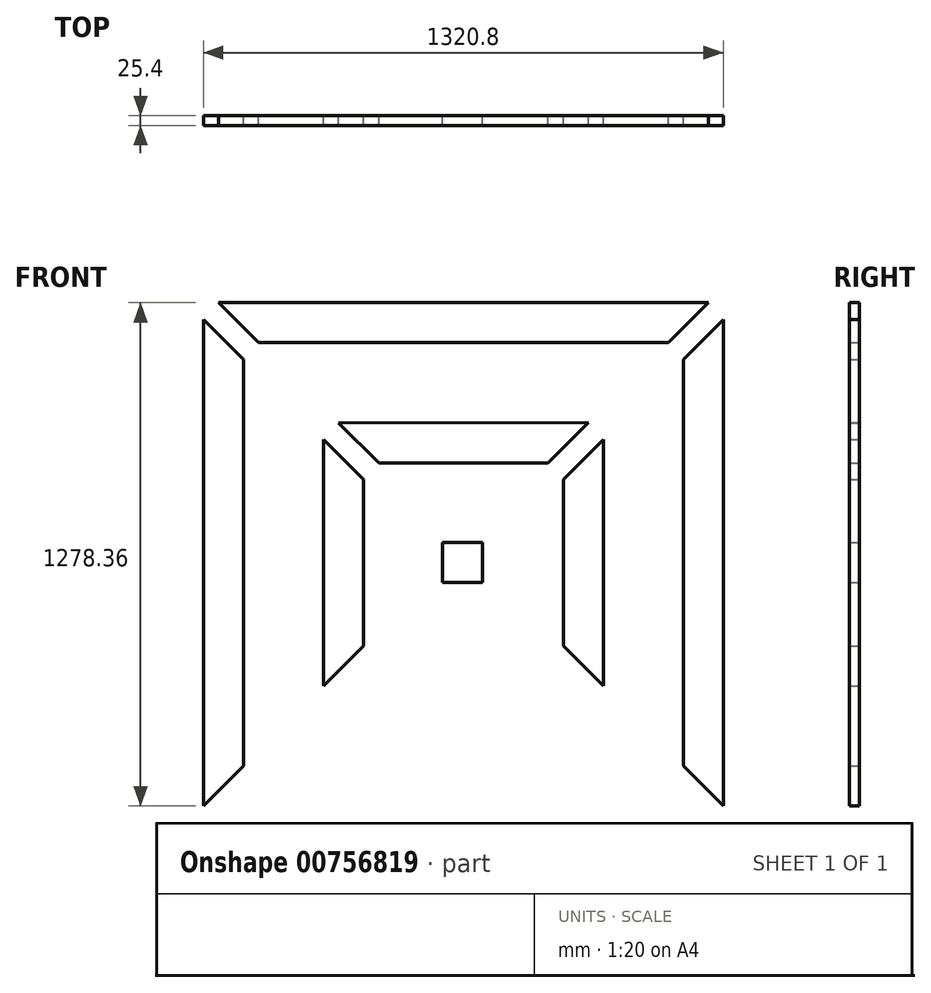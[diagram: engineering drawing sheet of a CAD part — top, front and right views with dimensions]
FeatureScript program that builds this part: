
annotation { "Feature Type Name" : "Feature", "Feature Type Description" : "" }
export const myFeature = defineFeature(function(context is Context, id is Id, definition is map)
    precondition{}
    {
        {
            var Q0;
            Q0=qCreatedBy(makeId("Front.planeOp"),FACE);
            var sketch = newSketch(context, id + "F0", { "sketchPlane" : qUnion([Q0])});
            skLineSegment(sketch, "E0.bottom", {"start": v(1332.07, -71.9) * mm, "end": v(1205.07, -71.9) * mm});
            skLineSegment(sketch, "E0.top", {"start": v(1332.07, -198.9) * mm, "end": v(1205.07, -198.9) * mm});
            skLineSegment(sketch, "E0.left", {"start": v(1332.07, -71.9) * mm, "end": v(1332.07, -198.9) * mm});
            skLineSegment(sketch, "E0.right", {"start": v(1205.07, -71.9) * mm, "end": v(1205.07, -198.9) * mm});
            skPoint(sketch, "E0.middle", {"position": v(1268.57, -135.4) * mm});
            skLineSegment(sketch, "E1", {"start": v(1268.57, -71.9) * mm, "end": v(1268.57, -46.5) * mm});
            skLineSegment(sketch, "E2", {"start": v(1268.57, -46.5) * mm, "end": v(1268.57, 80.5) * mm});
            skLineSegment(sketch, "E3", {"start": v(1268.57, 80.5) * mm, "end": v(1268.57, 105.9) * mm});
            skLineSegment(sketch, "E4", {"start": v(1205.07, -135.4) * mm, "end": v(1179.67, -135.4) * mm});
            skLineSegment(sketch, "E5", {"start": v(1179.67, -135.4) * mm, "end": v(1054.23, -135.4) * mm});
            skLineSegment(sketch, "E6", {"start": v(901.83, -135.4) * mm, "end": v(876.43, -135.4) * mm});
            skLineSegment(sketch, "E7", {"start": v(571.63, -135.4) * mm, "end": v(571.63, 563.1) * mm});
            skLineSegment(sketch, "E8", {"start": v(571.63, 563.1) * mm, "end": v(1268.57, 563.1) * mm});
            skLineSegment(sketch, "E9", {"start": v(1268.57, 537.7) * mm, "end": v(597.03, 537.7) * mm});
            skLineSegment(sketch, "E10", {"start": v(597.03, 537.7) * mm, "end": v(597.03, -135.4) * mm});
            skLineSegment(sketch, "E11", {"start": v(724.03, -135.4) * mm, "end": v(724.03, 410.7) * mm});
            skLineSegment(sketch, "E12", {"start": v(724.03, 410.7) * mm, "end": v(1268.57, 410.7) * mm});
            skLineSegment(sketch, "E13", {"start": v(1268.57, 385.3) * mm, "end": v(749.43, 385.3) * mm});
            skLineSegment(sketch, "E14", {"start": v(749.43, 385.3) * mm, "end": v(749.43, -135.4) * mm});
            skLineSegment(sketch, "E15", {"start": v(876.43, -135.4) * mm, "end": v(876.43, 258.3) * mm});
            skLineSegment(sketch, "E16", {"start": v(876.43, 258.3) * mm, "end": v(1268.57, 258.3) * mm});
            skLineSegment(sketch, "E17", {"start": v(1268.57, 232.9) * mm, "end": v(901.83, 232.9) * mm});
            skLineSegment(sketch, "E18", {"start": v(901.83, 232.9) * mm, "end": v(901.83, -135.4) * mm});
            skLineSegment(sketch, "E19", {"start": v(1028.83, -135.4) * mm, "end": v(1028.83, 105.9) * mm});
            skLineSegment(sketch, "E20", {"start": v(1028.83, 105.9) * mm, "end": v(1268.57, 105.9) * mm});
            skLineSegment(sketch, "E21", {"start": v(1268.57, 80.5) * mm, "end": v(1054.23, 80.5) * mm});
            skLineSegment(sketch, "E22", {"start": v(1054.23, 80.5) * mm, "end": v(1054.23, -135.4) * mm});
            skLineSegment(sketch, "E23", {"start": v(1179.67, -135.4) * mm, "end": v(1179.67, -46.5) * mm});
            skLineSegment(sketch, "E24", {"start": v(1179.67, -46.5) * mm, "end": v(1268.57, -46.5) * mm});
            skLineSegment(sketch, "E25", {"start": v(578.07, 533.09) * mm, "end": v(1181.32, -70.16) * mm});
            skLineSegment(sketch, "E26", {"start": v(1200.28, -46.5) * mm, "end": v(597.03, 556.74) * mm});
            skLineSegment(sketch, "E27.MirrorCS", {"start": v(1359.03, -46.5) * mm, "end": v(1270.13, -46.5) * mm});
            skLineSegment(sketch, "E28.MirrorCS", {"start": v(1339.98, -46.5) * mm, "end": v(1943.23, 556.74) * mm});
            skLineSegment(sketch, "E29.MirrorCS", {"start": v(1962.2, 533.09) * mm, "end": v(1358.94, -70.16) * mm});
            skLineSegment(sketch, "E30.MirrorCS", {"start": v(1270.13, 80.5) * mm, "end": v(1486.03, 80.5) * mm});
            skLineSegment(sketch, "E31.MirrorCS", {"start": v(1511.43, 105.9) * mm, "end": v(1270.13, 105.9) * mm});
            skLineSegment(sketch, "E32.MirrorCS", {"start": v(1270.13, 232.9) * mm, "end": v(1638.43, 232.9) * mm});
            skLineSegment(sketch, "E33.MirrorCS", {"start": v(1663.84, 258.3) * mm, "end": v(1270.14, 258.3) * mm});
            skLineSegment(sketch, "E34.MirrorCS", {"start": v(1270.14, 385.3) * mm, "end": v(1790.84, 385.3) * mm});
            skLineSegment(sketch, "E35.MirrorCS", {"start": v(1816.24, 410.7) * mm, "end": v(1270.14, 410.7) * mm});
            skLineSegment(sketch, "E36.MirrorCS", {"start": v(1270.13, 537.7) * mm, "end": v(1943.23, 537.7) * mm});
            skLineSegment(sketch, "E37.MirrorCS", {"start": v(1968.63, 563.1) * mm, "end": v(1270.13, 563.1) * mm});
            skLineSegment(sketch, "E38.MirrorCS", {"start": v(1968.63, -135.4) * mm, "end": v(1968.63, 563.1) * mm});
            skLineSegment(sketch, "E39.MirrorCS", {"start": v(1943.23, 537.7) * mm, "end": v(1943.23, -135.4) * mm});
            skLineSegment(sketch, "E40.MirrorCS", {"start": v(1663.83, -135.4) * mm, "end": v(1663.83, 258.3) * mm});
            skLineSegment(sketch, "E41.MirrorCS", {"start": v(1638.43, 232.9) * mm, "end": v(1638.43, -135.4) * mm});
            skLineSegment(sketch, "E42.MirrorCS", {"start": v(1511.43, -135.4) * mm, "end": v(1511.43, 105.9) * mm});
            skLineSegment(sketch, "E43.MirrorCS", {"start": v(1486.03, 80.5) * mm, "end": v(1486.03, -135.4) * mm});
            skLineSegment(sketch, "E44.MirrorCS", {"start": v(1359.03, -135.4) * mm, "end": v(1359.03, -46.5) * mm});
            skLineSegment(sketch, "E45.MirrorCS", {"start": v(1333.63, -71.9) * mm, "end": v(1333.63, -198.9) * mm});
            skLineSegment(sketch, "E46.MirrorCS", {"start": v(1790.83, 385.3) * mm, "end": v(1790.83, -135.4) * mm});
            skLineSegment(sketch, "E47.MirrorCS", {"start": v(1816.23, -135.4) * mm, "end": v(1816.23, 410.7) * mm});
            skLineSegment(sketch, "E48.MirrorCS", {"start": v(597.03, -808.5) * mm, "end": v(597.03, -135.4) * mm});
            skLineSegment(sketch, "E49.MirrorCS", {"start": v(724.03, -135.4) * mm, "end": v(724.03, -681.5) * mm});
            skLineSegment(sketch, "E50.MirrorCS", {"start": v(749.43, -656.1) * mm, "end": v(749.43, -135.4) * mm});
            skLineSegment(sketch, "E51.MirrorCS", {"start": v(876.43, -135.4) * mm, "end": v(876.43, -529.1) * mm});
            skLineSegment(sketch, "E52.MirrorCS", {"start": v(901.83, -503.7) * mm, "end": v(901.83, -135.4) * mm});
            skLineSegment(sketch, "E53.MirrorCS", {"start": v(1028.83, -135.4) * mm, "end": v(1028.83, -376.7) * mm});
            skLineSegment(sketch, "E54.MirrorCS", {"start": v(1054.23, -351.3) * mm, "end": v(1054.23, -135.4) * mm});
            skLineSegment(sketch, "E55.MirrorCS", {"start": v(1181.23, -135.4) * mm, "end": v(1181.23, -224.3) * mm});
            skLineSegment(sketch, "E56.MirrorCS", {"start": v(1206.63, -198.9) * mm, "end": v(1206.63, -71.9) * mm});
            skLineSegment(sketch, "E57.MirrorCS", {"start": v(1333.63, -198.9) * mm, "end": v(1333.63, -71.9) * mm});
            skLineSegment(sketch, "E58.MirrorCS", {"start": v(1359.03, -135.4) * mm, "end": v(1359.03, -224.3) * mm});
            skLineSegment(sketch, "E59.MirrorCS", {"start": v(1486.03, -351.3) * mm, "end": v(1486.03, -135.4) * mm});
            skLineSegment(sketch, "E60.MirrorCS", {"start": v(1511.43, -135.4) * mm, "end": v(1511.43, -376.7) * mm});
            skLineSegment(sketch, "E61.MirrorCS", {"start": v(1638.43, -503.7) * mm, "end": v(1638.43, -135.4) * mm});
            skLineSegment(sketch, "E62.MirrorCS", {"start": v(1663.83, -135.4) * mm, "end": v(1663.83, -529.1) * mm});
            skLineSegment(sketch, "E63.MirrorCS", {"start": v(1790.83, -656.1) * mm, "end": v(1790.83, -135.4) * mm});
            skLineSegment(sketch, "E64.MirrorCS", {"start": v(1816.23, -135.4) * mm, "end": v(1816.23, -681.5) * mm});
            skLineSegment(sketch, "E65.MirrorCS", {"start": v(1943.23, -808.5) * mm, "end": v(1943.23, -135.4) * mm});
            skLineSegment(sketch, "E66.MirrorCS", {"start": v(1968.63, -135.4) * mm, "end": v(1968.63, -833.9) * mm});
            skLineSegment(sketch, "E67.MirrorCS", {"start": v(1962.2, -803.9) * mm, "end": v(1358.94, -200.65) * mm});
            skLineSegment(sketch, "E68.MirrorCS", {"start": v(1339.98, -224.3) * mm, "end": v(1943.23, -827.56) * mm});
            skLineSegment(sketch, "E69.MirrorCS", {"start": v(578.07, -803.9) * mm, "end": v(1181.32, -200.65) * mm});
            skLineSegment(sketch, "E70.MirrorCS", {"start": v(1270.13, -351.3) * mm, "end": v(1054.23, -351.3) * mm});
            skLineSegment(sketch, "E71.MirrorCS", {"start": v(1270.13, -351.3) * mm, "end": v(1486.03, -351.3) * mm});
            skLineSegment(sketch, "E72.MirrorCS", {"start": v(1663.83, -529.1) * mm, "end": v(1270.13, -529.1) * mm});
            skLineSegment(sketch, "E73.MirrorCS", {"start": v(876.43, -529.1) * mm, "end": v(1270.13, -529.1) * mm});
            skLineSegment(sketch, "E74.MirrorCS", {"start": v(1270.13, -503.7) * mm, "end": v(901.83, -503.7) * mm});
            skLineSegment(sketch, "E75.MirrorCS", {"start": v(1270.13, -503.7) * mm, "end": v(1638.43, -503.7) * mm});
            skLineSegment(sketch, "E76.MirrorCS", {"start": v(1270.13, -656.1) * mm, "end": v(1790.83, -656.1) * mm});
            skLineSegment(sketch, "E77.MirrorCS", {"start": v(1270.13, -656.1) * mm, "end": v(749.43, -656.1) * mm});
            skLineSegment(sketch, "E78.MirrorCS", {"start": v(724.03, -681.5) * mm, "end": v(1270.13, -681.5) * mm});
            skLineSegment(sketch, "E79.MirrorCS", {"start": v(1816.23, -681.5) * mm, "end": v(1270.13, -681.5) * mm});
            skLineSegment(sketch, "E80.MirrorCS", {"start": v(1270.13, -808.5) * mm, "end": v(1943.23, -808.5) * mm});
            skLineSegment(sketch, "E81.MirrorCS", {"start": v(1968.63, -833.9) * mm, "end": v(1270.13, -833.9) * mm});
            skLineSegment(sketch, "E82.MirrorCS", {"start": v(571.63, -833.9) * mm, "end": v(1270.13, -833.9) * mm});
            skLineSegment(sketch, "E83.MirrorCS", {"start": v(1270.13, -808.5) * mm, "end": v(597.03, -808.5) * mm});
            skLineSegment(sketch, "E84.MirrorCS", {"start": v(571.63, -135.4) * mm, "end": v(571.63, -833.9) * mm});
            skLineSegment(sketch, "E85.MirrorCS", {"start": v(1028.83, -376.7) * mm, "end": v(1270.13, -376.7) * mm});
            skLineSegment(sketch, "E86.MirrorCS", {"start": v(1511.43, -376.7) * mm, "end": v(1270.13, -376.7) * mm});
            skLineSegment(sketch, "E87.MirrorCS", {"start": v(1200.28, -224.3) * mm, "end": v(597.03, -827.56) * mm});
            skLineSegment(sketch, "E88.MirrorCS", {"start": v(1359.03, -224.3) * mm, "end": v(1270.13, -224.3) * mm});
            skLineSegment(sketch, "E89.MirrorCS", {"start": v(1181.23, -224.3) * mm, "end": v(1270.13, -224.3) * mm});
            skLineSegment(sketch, "E90", {"start": v(596.66, 514.5) * mm, "end": v(597.03, 495.46) * mm});
            skLineSegment(sketch, "E91", {"start": v(616.08, 537.7) * mm, "end": v(635.13, 537.48) * mm});
            skLineSegment(sketch, "E92", {"start": v(1047.88, 105.9) * mm, "end": v(1066.93, 105.9) * mm});
            skLineSegment(sketch, "E93", {"start": v(1028.83, 82.33) * mm, "end": v(1028.83, 63.28) * mm});
            skLineSegment(sketch, "E94", {"start": v(1028.83, 63.28) * mm, "end": v(597.03, 495.46) * mm});
            skLineSegment(sketch, "E95", {"start": v(635.13, 537.48) * mm, "end": v(1066.93, 105.9) * mm});
            skLineSegment(sketch, "E96", {"start": v(635.13, 537.48) * mm, "end": v(635.13, 518.64) * mm});
            skLineSegment(sketch, "E97", {"start": v(724.03, 368.34) * mm, "end": v(711.33, 368.34) * mm});
            skLineSegment(sketch, "E98", {"start": v(597.03, 495.46) * mm, "end": v(609.73, 495.46) * mm});
            skLineSegment(sketch, "E99", {"start": v(609.73, 495.46) * mm, "end": v(609.73, -135.4) * mm});
            skLineSegment(sketch, "E100", {"start": v(571.63, 563.1) * mm, "end": v(1205.07, -71.9) * mm});
            skLineSegment(sketch, "E101.bottom", {"start": v(1205.07, -71.9) * mm, "end": v(1217.77, -71.9) * mm});
            skLineSegment(sketch, "E101.top", {"start": v(1205.07, -84.6) * mm, "end": v(1217.77, -84.6) * mm});
            skLineSegment(sketch, "E101.left", {"start": v(1205.07, -71.9) * mm, "end": v(1205.07, -84.6) * mm});
            skLineSegment(sketch, "E101.right", {"start": v(1217.77, -71.9) * mm, "end": v(1217.77, -84.6) * mm});
            skLineSegment(sketch, "E102.bottom", {"start": v(1217.77, -84.6) * mm, "end": v(1268.57, -84.6) * mm});
            skLineSegment(sketch, "E102.top", {"start": v(1217.77, -135.4) * mm, "end": v(1268.57, -135.4) * mm});
            skLineSegment(sketch, "E102.left", {"start": v(1217.77, -84.6) * mm, "end": v(1217.77, -135.4) * mm});
            skLineSegment(sketch, "E102.right", {"start": v(1268.57, -84.6) * mm, "end": v(1268.57, -135.4) * mm});
            skLineSegment(sketch, "E103", {"start": v(1028.83, 63.28) * mm, "end": v(1016.13, 63.28) * mm});
            skLineSegment(sketch, "E104", {"start": v(1016.13, 63.28) * mm, "end": v(1016.13, 75.99) * mm});
            skLineSegment(sketch, "E105", {"start": v(1016.13, 75.99) * mm, "end": v(1016.13, -135.4) * mm});
            skLineSegment(sketch, "E106", {"start": v(901.83, 169.52) * mm, "end": v(914.53, 169.52) * mm});
            skLineSegment(sketch, "E107", {"start": v(914.53, 169.52) * mm, "end": v(914.53, 184.76) * mm});
            skLineSegment(sketch, "E108", {"start": v(914.53, 184.76) * mm, "end": v(914.53, -135.4) * mm});
            skLineSegment(sketch, "E109.MirrorCS", {"start": v(753.67, 423.4) * mm, "end": v(1270.13, 423.4) * mm});
            skLineSegment(sketch, "E110.MirrorCS", {"start": v(1217.73, -84.64) * mm, "end": v(1268.53, -84.76) * mm});
            skLineSegment(sketch, "E111.bottom", {"start": v(1332.07, -198.9) * mm, "end": v(1319.37, -198.9) * mm});
            skLineSegment(sketch, "E111.top", {"start": v(1332.07, -186.2) * mm, "end": v(1319.37, -186.2) * mm});
            skLineSegment(sketch, "E111.left", {"start": v(1332.07, -198.9) * mm, "end": v(1332.07, -186.2) * mm});
            skLineSegment(sketch, "E111.right", {"start": v(1319.37, -198.9) * mm, "end": v(1319.37, -186.2) * mm});
            skLineSegment(sketch, "E112.bottom", {"start": v(1217.77, -84.6) * mm, "end": v(1319.37, -84.6) * mm});
            skLineSegment(sketch, "E112.top", {"start": v(1217.77, -186.2) * mm, "end": v(1319.37, -186.2) * mm});
            skLineSegment(sketch, "E112.left", {"start": v(1217.77, -84.6) * mm, "end": v(1217.77, -186.2) * mm});
            skLineSegment(sketch, "E112.right", {"start": v(1319.37, -84.6) * mm, "end": v(1319.37, -186.2) * mm});
            skLineSegment(sketch, "E113.MirrorCS", {"start": v(1905.13, 537.48) * mm, "end": v(1473.33, 105.9) * mm});
            skLineSegment(sketch, "E114.MirrorCS", {"start": v(1786.6, 423.4) * mm, "end": v(1270.13, 423.4) * mm});
            skLineSegment(sketch, "E115.MirrorCS", {"start": v(1930.53, 495.46) * mm, "end": v(1930.53, -135.4) * mm});
            skLineSegment(sketch, "E116.MirrorCS", {"start": v(1828.93, 381.06) * mm, "end": v(1828.93, -135.4) * mm});
            skLineSegment(sketch, "E117.MirrorCS", {"start": v(1625.73, 184.76) * mm, "end": v(1625.73, -135.4) * mm});
            skLineSegment(sketch, "E118.MirrorCS", {"start": v(1524.13, 75.99) * mm, "end": v(1524.13, -135.4) * mm});
            skLineSegment(sketch, "E119.MirrorCS", {"start": v(1511.43, 63.28) * mm, "end": v(1943.23, 495.46) * mm});
            skLineSegment(sketch, "E120.MirrorCS", {"start": v(609.73, -766.27) * mm, "end": v(609.73, -135.4) * mm});
            skLineSegment(sketch, "E121.MirrorCS", {"start": v(711.33, -651.87) * mm, "end": v(711.33, -135.4) * mm});
            skLineSegment(sketch, "E122.MirrorCS", {"start": v(914.53, -455.58) * mm, "end": v(914.53, -135.4) * mm});
            skLineSegment(sketch, "E123.MirrorCS", {"start": v(1016.13, -346.8) * mm, "end": v(1016.13, -135.4) * mm});
            skLineSegment(sketch, "E124.MirrorCS", {"start": v(1524.13, -346.8) * mm, "end": v(1524.13, -135.4) * mm});
            skLineSegment(sketch, "E125.MirrorCS", {"start": v(1625.73, -455.58) * mm, "end": v(1625.73, -135.4) * mm});
            skLineSegment(sketch, "E126.MirrorCS", {"start": v(1828.93, -651.87) * mm, "end": v(1828.93, -135.4) * mm});
            skLineSegment(sketch, "E127.MirrorCS", {"start": v(1930.53, -766.27) * mm, "end": v(1930.53, -135.4) * mm});
            skLineSegment(sketch, "E128.MirrorCS", {"start": v(1028.83, -334.09) * mm, "end": v(597.03, -766.27) * mm});
            skLineSegment(sketch, "E129.MirrorCS", {"start": v(1511.43, -334.09) * mm, "end": v(1943.23, -766.27) * mm});
            skLineSegment(sketch, "E130.MirrorCS", {"start": v(1905.13, -808.3) * mm, "end": v(1473.33, -376.7) * mm});
            skLineSegment(sketch, "E131.MirrorCS", {"start": v(635.13, -808.3) * mm, "end": v(1066.93, -376.7) * mm});
            skLineSegment(sketch, "E132.MirrorCS", {"start": v(1058.74, -389.4) * mm, "end": v(1270.13, -389.4) * mm});
            skLineSegment(sketch, "E133.MirrorCS", {"start": v(1481.53, -389.4) * mm, "end": v(1270.13, -389.4) * mm});
            skLineSegment(sketch, "E134.MirrorCS", {"start": v(949.96, -491) * mm, "end": v(1270.13, -491) * mm});
            skLineSegment(sketch, "E135.MirrorCS", {"start": v(1590.3, -491) * mm, "end": v(1270.13, -491) * mm});
            skLineSegment(sketch, "E136.MirrorCS", {"start": v(753.67, -694.2) * mm, "end": v(1270.13, -694.2) * mm});
            skLineSegment(sketch, "E137.MirrorCS", {"start": v(1786.6, -694.2) * mm, "end": v(1270.13, -694.2) * mm});
            skLineSegment(sketch, "E138.MirrorCS", {"start": v(639.27, -795.8) * mm, "end": v(1270.13, -795.8) * mm});
            skLineSegment(sketch, "E139.MirrorCS", {"start": v(1901, -795.8) * mm, "end": v(1270.13, -795.8) * mm});
            skLineSegment(sketch, "E140", {"start": v(711.33, -135.4) * mm, "end": v(711.33, 381.06) * mm});
            skLineSegment(sketch, "E141", {"start": v(1054.23, -389.4) * mm, "end": v(1486.04, -389.4) * mm});
            skLineSegment(sketch, "E142", {"start": v(749.28, -694.2) * mm, "end": v(1790.99, -694.2) * mm});
            skLineSegment(sketch, "E143", {"start": v(1055.43, 117.4) * mm, "end": v(1484.84, 117.4) * mm});
            skLineSegment(sketch, "E144", {"start": v(1790.99, 423.4) * mm, "end": v(749.28, 423.4) * mm});
            skLineSegment(sketch, "E145", {"start": v(953.52, 219.25) * mm, "end": v(1587.69, 220.2) * mm});
            skLineSegment(sketch, "E146", {"start": v(1268.57, 232.9) * mm, "end": v(1270.13, 232.9) * mm});
            skLineSegment(sketch, "E147", {"start": v(1268.57, 258.3) * mm, "end": v(1270.14, 258.3) * mm});
            skLineSegment(sketch, "E148", {"start": v(1268.57, 385.3) * mm, "end": v(1270.14, 385.3) * mm});
            skLineSegment(sketch, "E149", {"start": v(1268.57, 410.7) * mm, "end": v(1270.14, 410.7) * mm});
            skLineSegment(sketch, "E150", {"start": v(647.82, 524.8) * mm, "end": v(1892.45, 524.8) * mm});
            skSolve(sketch);
        }
        {
            var Q0;
            {var subQ5=sQuery(id+"F0.wireOp",EDGE,"E121.MirrorCS");Q0=makeQuery(id+"F0.imprint","IMPRINT",FACE,{"disambiguationData":[TD([[makeQuery(id+"F0.imprint","IMPRINT",EDGE,{"derivedFrom":subQ5}),1.0]])]});}
            var Q1;
            {var subQ5=sQuery(id+"F0.wireOp",EDGE,"E102.top");Q1=makeQuery(id+"F0.imprint","IMPRINT",FACE,{"disambiguationData":[TD([[makeQuery(id+"F0.imprint","IMPRINT",EDGE,{"derivedFrom":subQ5}),1.0]])]});}
            var Q2;
            {var subQ4=sQuery(id+"F0.wireOp",EDGE,"E102.top");Q2=makeQuery(id+"F0.imprint","IMPRINT",FACE,{"disambiguationData":[TD([[makeQuery(id+"F0.imprint","IMPRINT",EDGE,{"derivedFrom":subQ4}),-1.0]])]});}
            var Q3;
            {var subQ6=sQuery(id+"F0.wireOp",EDGE,"E123.MirrorCS");Q3=makeQuery(id+"F0.imprint","IMPRINT",FACE,{"disambiguationData":[TD([[makeQuery(id+"F0.imprint","IMPRINT",EDGE,{"derivedFrom":subQ6}),1.0]])]});}
            var Q4;
            {var subQ5=sQuery(id+"F0.wireOp",EDGE,"E141");var subQ10=makeQuery(id+"F0.imprint","IMPRINT",VERTEX,{"disambiguationData":[OD(0.0)],"derivedFrom":subQ5});Q4=makeQuery(id+"F0.imprint","IMPRINT",FACE,{"disambiguationData":[TD([[makeQuery(id+"F0.imprint","IMPRINT",EDGE,{"disambiguationData":[TD([[subQ10,-1.0]])],"derivedFrom":subQ5}),-1.0]])]});}
            var Q5;
            {var subQ1=sQuery(id+"F0.wireOp",EDGE,"E118.MirrorCS");Q5=makeQuery(id+"F0.imprint","IMPRINT",FACE,{"disambiguationData":[TD([[makeQuery(id+"F0.imprint","IMPRINT",EDGE,{"derivedFrom":subQ1}),1.0]])]});}
            var Q6;
            {var subQ0=sQuery(id+"F0.wireOp",EDGE,"E143");Q6=makeQuery(id+"F0.imprint","IMPRINT",FACE,{"disambiguationData":[TD([[makeQuery(id+"F0.imprint","IMPRINT",EDGE,{"derivedFrom":subQ0}),1.0]])]});}
            var Q7;
            {var subQ2=sQuery(id+"F0.wireOp",EDGE,"E116.MirrorCS");Q7=makeQuery(id+"F0.imprint","IMPRINT",FACE,{"disambiguationData":[TD([[makeQuery(id+"F0.imprint","IMPRINT",EDGE,{"derivedFrom":subQ2}),1.0]])]});}
            var Q8;
            {var subQ5=sQuery(id+"F0.wireOp",EDGE,"E142");var subQ10=makeQuery(id+"F0.imprint","IMPRINT",VERTEX,{"disambiguationData":[OD(0.0)],"derivedFrom":subQ5});Q8=makeQuery(id+"F0.imprint","IMPRINT",FACE,{"disambiguationData":[TD([[makeQuery(id+"F0.imprint","IMPRINT",EDGE,{"disambiguationData":[TD([[subQ10,-1.0]])],"derivedFrom":subQ5}),-1.0]])]});}
            var Q9;
            {var subQ5=sQuery(id+"F0.wireOp",EDGE,"E150");Q9=makeQuery(id+"F0.imprint","IMPRINT",FACE,{"disambiguationData":[TD([[makeQuery(id+"F0.imprint","IMPRINT",EDGE,{"derivedFrom":subQ5}),-1.0]])]});}
            extrude(context, id + "F1", {"entities" : qUnion([Q0, Q1, Q2, Q3, Q4, Q5, Q6, Q7, Q8, Q9]), "depth" : 25.4 * mm, "offsetDistance" : 25.4 * mm});
        }
    });
